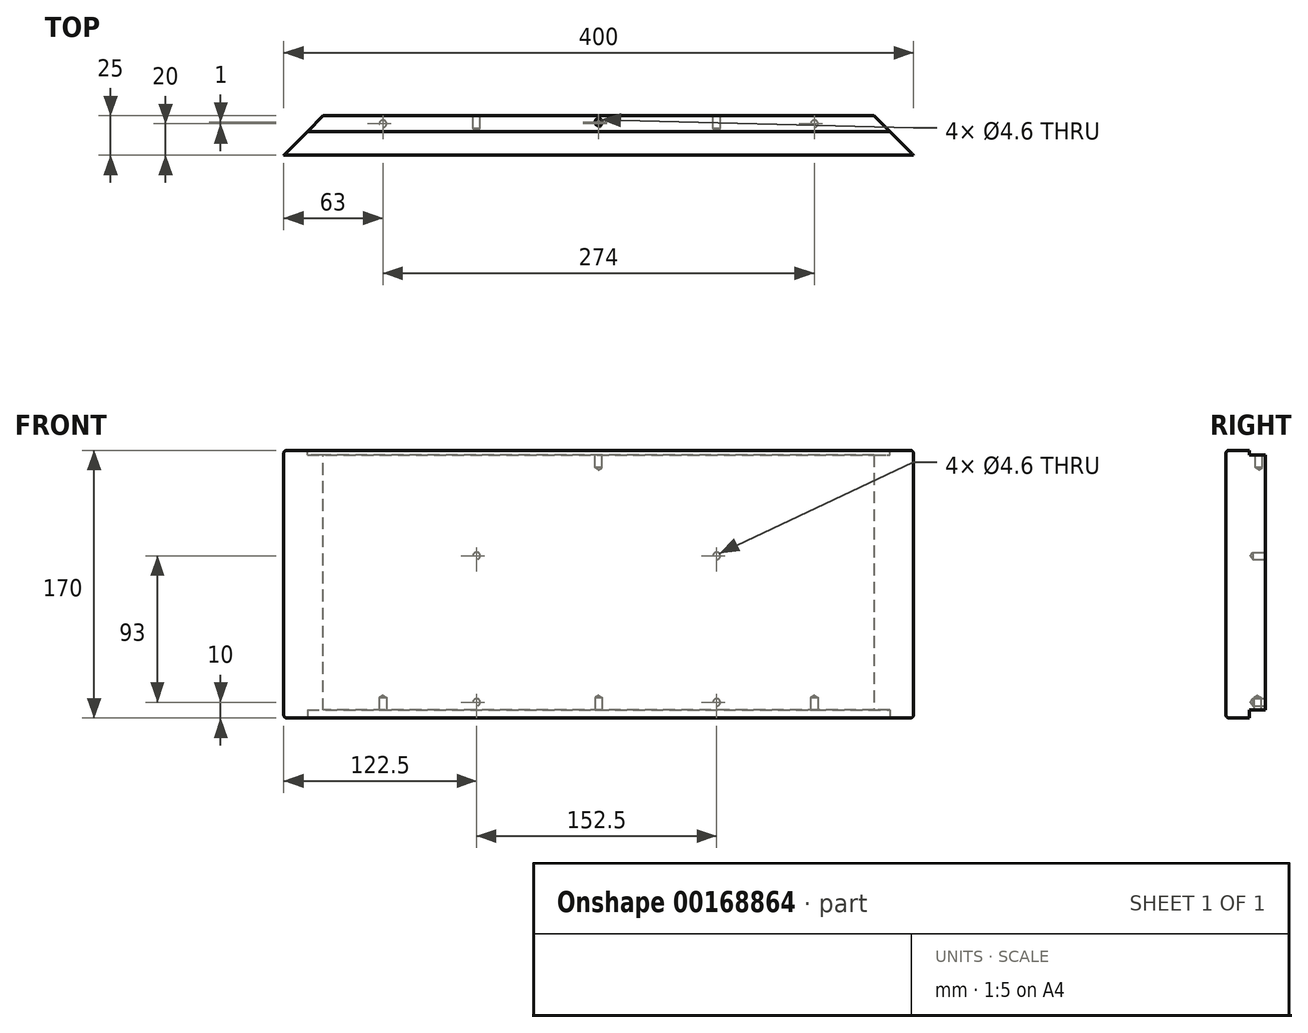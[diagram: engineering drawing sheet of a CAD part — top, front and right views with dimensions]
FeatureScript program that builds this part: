
annotation { "Feature Type Name" : "Feature", "Feature Type Description" : "" }
export const myFeature = defineFeature(function(context is Context, id is Id, definition is map)
    precondition{}
    {
        {
            var Q0;
            Q0=qCreatedBy(makeId("Front.planeOp"),FACE);
            var sketch = newSketch(context, id + "F0", { "sketchPlane" : qUnion([Q0])});
            skLineSegment(sketch, "E0.bottom", {"start": v(200, -85) * mm, "end": v(-200, -85) * mm});
            skLineSegment(sketch, "E0.top", {"start": v(200, 85) * mm, "end": v(-200, 85) * mm});
            skLineSegment(sketch, "E0.left", {"start": v(200, -85) * mm, "end": v(200, 85) * mm});
            skLineSegment(sketch, "E0.right", {"start": v(-200, -85) * mm, "end": v(-200, 85) * mm});
            skPoint(sketch, "E0.middle", {"position": v(0, 0) * mm});
            skSolve(sketch);
        }
        {
            var Q0;
            Q0=makeQuery(id+"F0.imprint","IMPRINT",FACE,{"disambiguationData":[TD([[makeQuery(id+"F0.imprint","IMPRINT",EDGE,{"derivedFrom":sQuery(id+"F0.wireOp",EDGE,"E0.bottom")}),-1.0]])]});
            extrude(context, id + "F1", {"entities" : qUnion([Q0]), "depth" : 25 * mm});
        }
        {
            var Q0;
            Q0=makeQuery(id+"F1.opExtrude","CAP_EDGE",EDGE,{"disambiguationData":[OSD([sQuery(id+"F0.wireOp",EDGE,"E0.right")])],"isStart":true});
            var Q1;
            Q1=makeQuery(id+"F1.opExtrude","CAP_EDGE",EDGE,{"disambiguationData":[OSD([sQuery(id+"F0.wireOp",EDGE,"E0.left")])],"isStart":true});
            chamfer(context, id + "F2", {"entities" : qUnion([Q0, Q1]), "width" : 25 * mm, "tangentPropagation" : true});
        }
        {
            var Q0;
            Q0=makeQuery(id+"F1.opExtrude","SWEPT_FACE",FACE,{"disambiguationData":[OSD([sQuery(id+"F0.wireOp",EDGE,"E0.top")])]});
            var sketch = newSketch(context, id + "F3", { "sketchPlane" : qUnion([Q0])});
            skLineSegment(sketch, "E1", {"start": v(-185, -10) * mm, "end": v(185, -10) * mm});
            skSolve(sketch);
        }
        {
            var Q0;
            {var subQ0=sQuery(id+"F3.wireOp",EDGE,"E1");Q0=makeQuery(id+"F3.imprint","IMPRINT",FACE,{"disambiguationData":[TD([[makeQuery(id+"F3.imprint","IMPRINT",EDGE,{"derivedFrom":subQ0}),1.0]])]});}
            extrude(context, id + "F4", {"entities" : qUnion([Q0]), "operationType" : NewBodyOperationType.REMOVE, "oppositeDirection" : true, "depth" : 3 * mm});
        }
        {
            var Q0;
            Q0=makeQuery(id+"F1.opExtrude","SWEPT_FACE",FACE,{"disambiguationData":[OSD([sQuery(id+"F0.wireOp",EDGE,"E0.bottom")])]});
            var sketch = newSketch(context, id + "F5", { "sketchPlane" : qUnion([Q0])});
            skLineSegment(sketch, "E2", {"start": v(-185, 10) * mm, "end": v(185, 10) * mm});
            skSolve(sketch);
        }
        {
            var Q0;
            {var subQ0=sQuery(id+"F5.wireOp",EDGE,"E2");Q0=makeQuery(id+"F5.imprint","IMPRINT",FACE,{"disambiguationData":[TD([[makeQuery(id+"F5.imprint","IMPRINT",EDGE,{"derivedFrom":subQ0}),-1.0]])]});}
            extrude(context, id + "F6", {"entities" : qUnion([Q0]), "operationType" : NewBodyOperationType.REMOVE, "oppositeDirection" : true, "depth" : 5 * mm});
        }
        {
            var Q0;
            Q0=makeQuery(id+"F0.imprint","IMPRINT",FACE,{"disambiguationData":[TD([[makeQuery(id+"F0.imprint","IMPRINT",EDGE,{"derivedFrom":sQuery(id+"F0.wireOp",EDGE,"E0.bottom")}),-1.0]])]});
            var sketch = newSketch(context, id + "F7", { "sketchPlane" : qUnion([Q0])});
            skLineSegment(sketch, "E3", {"start": v(103.78, 18) * mm, "end": v(-103.59, 18) * mm, "construction": true});
            skLineSegment(sketch, "E4", {"start": v(107.53, -75) * mm, "end": v(-106.25, -75) * mm, "construction": true});
            skLineSegment(sketch, "E5", {"start": v(-77.5, 51.89) * mm, "end": v(-77.5, -54.68) * mm, "construction": true});
            skLineSegment(sketch, "E6", {"start": v(75, 48.14) * mm, "end": v(75, -53.83) * mm, "construction": true});
            skPoint(sketch, "E7", {"position": v(75, 18) * mm});
            skPoint(sketch, "E8", {"position": v(-77.5, 18) * mm});
            skPoint(sketch, "E9", {"position": v(-77.5, -75) * mm});
            skPoint(sketch, "E10", {"position": v(75, -75) * mm});
            skSolve(sketch);
        }
        {
            var Q0;
            Q0=sQuery(id+"F7.wireOp",VERTEX,"E7");
            var Q1;
            Q1=sQuery(id+"F7.wireOp",VERTEX,"E8");
            var Q2;
            Q2=sQuery(id+"F7.wireOp",VERTEX,"E9");
            var Q3;
            Q3=sQuery(id+"F7.wireOp",VERTEX,"E10");
            var Q4;
            Q4=makeQuery(id+"F1.opExtrude","SWEPT_BODY",BODY,{"disambiguationData":[OSD([sQuery(id+"F0.wireOp",EDGE,"E0.bottom"),sQuery(id+"F0.wireOp",EDGE,"E0.top"),sQuery(id+"F0.wireOp",EDGE,"E0.left"),sQuery(id+"F0.wireOp",EDGE,"E0.right")])]});
            hole(context, id + "F8", {"style" : HoleStyle.SIMPLE, "endStyle" : HoleEndStyle.BLIND, "oppositeDirection" : true, "holeDiameter" : 4.6 * mm, "holeDepth" : 8 * mm, "startFromSketch" : true, "locations" : qUnion([Q0, Q1, Q2, Q3]), "scope" : qUnion([Q4])});
        }
        {
            var Q0;
            Q0=makeQuery(id+"F4.boolean.opBoolean","COPY",FACE,{"derivedFrom":makeQuery(id+"F4.opExtrude","CAP_FACE",FACE,{"disambiguationData":[OSD([sQuery(id+"F0.wireOp",EDGE,"E0.top"),sQuery(id+"F0.wireOp",EDGE,"E0.left"),sQuery(id+"F0.wireOp",EDGE,"E0.right"),sQuery(id+"F3.wireOp",EDGE,"E1")])],"isStart":false})});
            var sketch = newSketch(context, id + "F9", { "sketchPlane" : qUnion([Q0])});
            skLineSegment(sketch, "E11", {"start": v(-176.3, -4) * mm, "end": v(171.3, -4) * mm, "construction": true});
            skPoint(sketch, "E11.endSnap0", {"position": v(161, -4) * mm});
            skLineSegment(sketch, "E12", {"start": v(0, 9.88) * mm, "end": v(0, -18.63) * mm, "construction": true});
            skPoint(sketch, "E13", {"position": v(0, -4) * mm});
            skSolve(sketch);
        }
        {
            var Q0;
            Q0=sQuery(id+"F9.wireOp",VERTEX,"E13");
            var Q1;
            Q1=makeQuery(id+"F1.opExtrude","SWEPT_BODY",BODY,{"disambiguationData":[OSD([sQuery(id+"F0.wireOp",EDGE,"E0.bottom"),sQuery(id+"F0.wireOp",EDGE,"E0.top"),sQuery(id+"F0.wireOp",EDGE,"E0.left"),sQuery(id+"F0.wireOp",EDGE,"E0.right")])]});
            hole(context, id + "F10", {"style" : HoleStyle.SIMPLE, "endStyle" : HoleEndStyle.BLIND, "holeDiameter" : 4.6 * mm, "holeDepth" : 8 * mm, "startFromSketch" : true, "locations" : qUnion([Q0]), "scope" : qUnion([Q1])});
        }
        {
            var Q0;
            Q0=makeQuery(id+"F6.boolean.opBoolean","COPY",FACE,{"derivedFrom":makeQuery(id+"F6.opExtrude","CAP_FACE",FACE,{"disambiguationData":[OSD([sQuery(id+"F0.wireOp",EDGE,"E0.bottom"),sQuery(id+"F0.wireOp",EDGE,"E0.left"),sQuery(id+"F0.wireOp",EDGE,"E0.right"),sQuery(id+"F5.wireOp",EDGE,"E2")])],"isStart":false})});
            var sketch = newSketch(context, id + "F11", { "sketchPlane" : qUnion([Q0])});
            skLineSegment(sketch, "E14", {"start": v(-174.3, 5) * mm, "end": v(174.8, 5) * mm, "construction": true});
            skLineSegment(sketch, "E15", {"start": v(0, 29.38) * mm, "end": v(0, -11.13) * mm, "construction": true});
            skPoint(sketch, "E15.endSnap0", {"position": v(0, 0) * mm});
            skLineSegment(sketch, "E16", {"start": v(137, 21.38) * mm, "end": v(137, -13.88) * mm, "construction": true});
            skLineSegment(sketch, "E17", {"start": v(-137, 23.63) * mm, "end": v(-137, -11.13) * mm, "construction": true});
            skPoint(sketch, "E18", {"position": v(-137, 5) * mm});
            skPoint(sketch, "E19", {"position": v(0, 5) * mm});
            skPoint(sketch, "E20", {"position": v(137, 5) * mm});
            skSolve(sketch);
        }
        {
            var Q0;
            Q0=sQuery(id+"F11.wireOp",VERTEX,"E18");
            var Q1;
            Q1=sQuery(id+"F11.wireOp",VERTEX,"E19");
            var Q2;
            Q2=sQuery(id+"F11.wireOp",VERTEX,"E20");
            var Q3;
            Q3=makeQuery(id+"F1.opExtrude","SWEPT_BODY",BODY,{"disambiguationData":[OSD([sQuery(id+"F0.wireOp",EDGE,"E0.bottom"),sQuery(id+"F0.wireOp",EDGE,"E0.top"),sQuery(id+"F0.wireOp",EDGE,"E0.left"),sQuery(id+"F0.wireOp",EDGE,"E0.right")])]});
            hole(context, id + "F12", {"style" : HoleStyle.SIMPLE, "endStyle" : HoleEndStyle.BLIND, "holeDiameter" : 4.6 * mm, "holeDepth" : 8 * mm, "startFromSketch" : true, "locations" : qUnion([Q0, Q1, Q2]), "scope" : qUnion([Q3])});
        }
        {
            var Q0;
            Q0=makeQuery(id+"F1.opExtrude","CAP_EDGE",EDGE,{"disambiguationData":[OSD([sQuery(id+"F0.wireOp",EDGE,"E0.top")])],"isStart":false});
            var Q1;
            Q1=makeQuery(id+"F1.opExtrude","CAP_EDGE",EDGE,{"disambiguationData":[OSD([sQuery(id+"F0.wireOp",EDGE,"E0.bottom")])],"isStart":false});
            fillet(context, id + "F13", {"entities" : qUnion([Q0, Q1]), "radius" : 2 * mm, "tangentPropagation" : true, "allowEdgeOverflow" : false});
        }
    });
